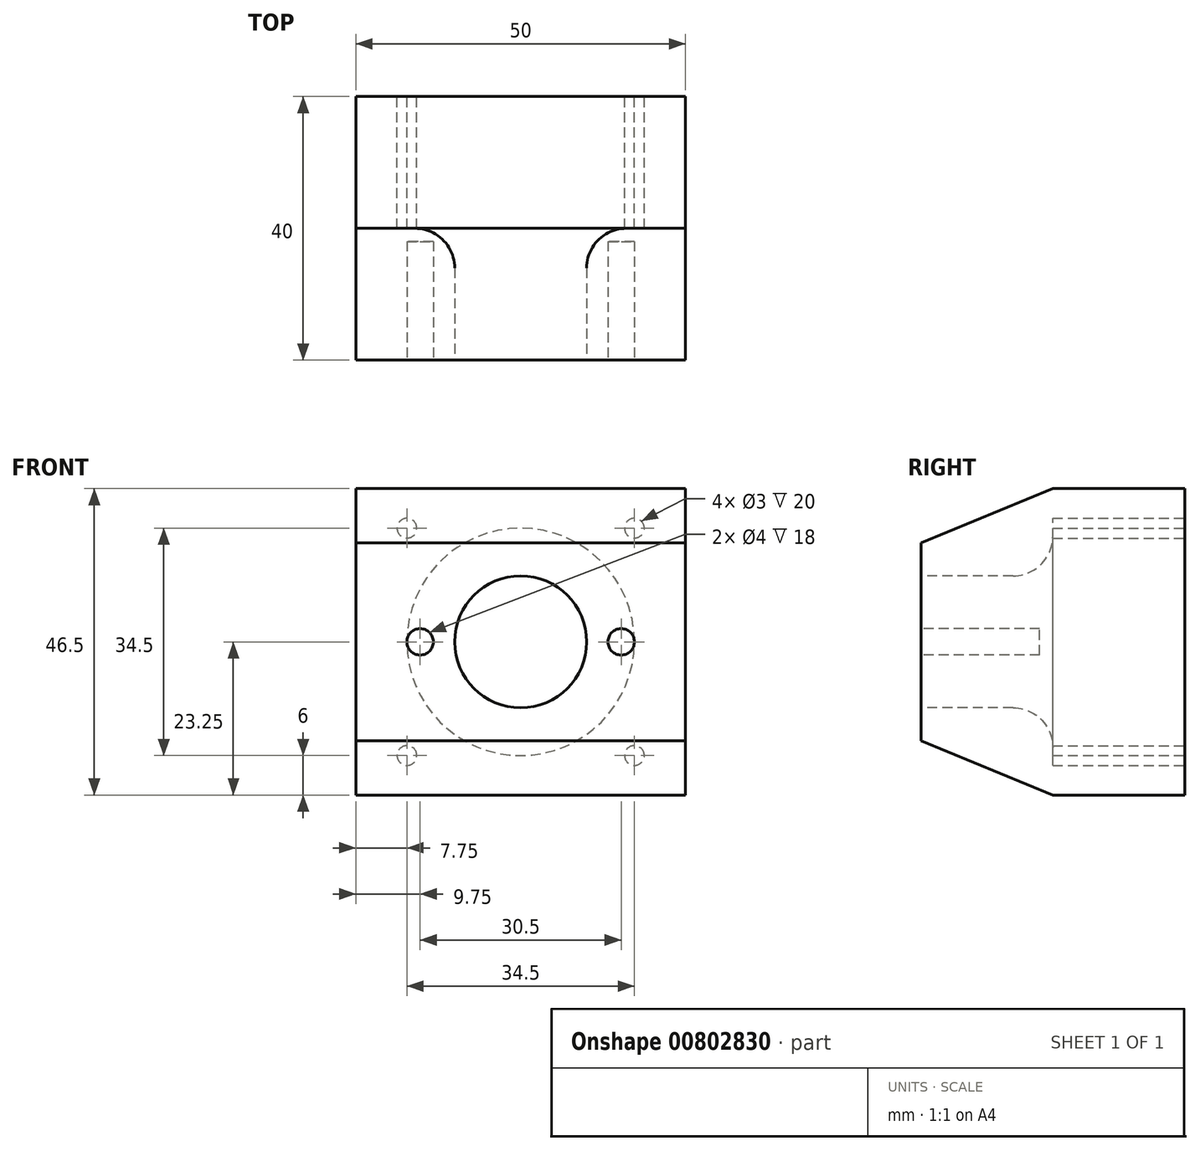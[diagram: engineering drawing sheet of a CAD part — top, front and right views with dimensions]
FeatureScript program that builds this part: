
annotation { "Feature Type Name" : "Feature", "Feature Type Description" : "" }
export const myFeature = defineFeature(function(context is Context, id is Id, definition is map)
    precondition{}
    {
        {
            var Q0;
            Q0=qCreatedBy(makeId("Front.planeOp"),FACE);
            var sketch = newSketch(context, id + "F0", { "sketchPlane" : qUnion([Q0])});
            skLineSegment(sketch, "E0.bottom", {"start": v(17.25, -17.25) * mm, "end": v(-17.25, -17.25) * mm});
            skLineSegment(sketch, "E0.top", {"start": v(17.25, 17.25) * mm, "end": v(-17.25, 17.25) * mm});
            skLineSegment(sketch, "E0.left", {"start": v(17.25, -17.25) * mm, "end": v(17.25, 17.25) * mm});
            skLineSegment(sketch, "E0.right", {"start": v(-17.25, -17.25) * mm, "end": v(-17.25, 17.25) * mm});
            skPoint(sketch, "E0.middle", {"position": v(0, 0) * mm});
            skCircle(sketch, "E1", {"center": v(-17.25, -17.25) * mm, "radius": 1.5 * mm});
            skCircle(sketch, "E2", {"center": v(17.25, -17.25) * mm, "radius": 1.5 * mm});
            skCircle(sketch, "E3", {"center": v(-17.25, 17.25) * mm, "radius": 1.5 * mm});
            skCircle(sketch, "E4", {"center": v(17.25, 17.25) * mm, "radius": 1.5 * mm});
            skLineSegment(sketch, "E5.bottom", {"start": v(23.25, -23.25) * mm, "end": v(-23.25, -23.25) * mm});
            skLineSegment(sketch, "E5.top", {"start": v(23.25, 23.25) * mm, "end": v(-23.25, 23.25) * mm});
            skLineSegment(sketch, "E5.left", {"start": v(23.25, -23.25) * mm, "end": v(23.25, 23.25) * mm});
            skLineSegment(sketch, "E5.right", {"start": v(-23.25, -23.25) * mm, "end": v(-23.25, 23.25) * mm});
            skCircle(sketch, "E6", {"center": v(0, 0) * mm, "radius": 17.25 * mm});
            skSolve(sketch);
        }
        {
            var Q0;
            Q0=makeQuery(id+"F0.imprint","IMPRINT",FACE,{"disambiguationData":[TD([[makeQuery(id+"F0.imprint","IMPRINT",EDGE,{"derivedFrom":sQuery(id+"F0.wireOp",EDGE,"E5.bottom")}),-1.0]])]});
            var Q1;
            {var subQ0=sQuery(id+"F0.wireOp",EDGE,"E6");var subQ1=sQuery(id+"F0.wireOp",EDGE,"E0.top");var subQ2=makeQuery(id+"F0.imprint","INTERSECT",VERTEX,{"derivedFrom":[subQ1,subQ0]});Q1=makeQuery(id+"F0.imprint","IMPRINT",FACE,{"disambiguationData":[TD([[makeQuery(id+"F0.imprint","IMPRINT",EDGE,{"disambiguationData":[TD([[subQ2,-1.0]])],"derivedFrom":subQ1}),1.0]])]});}
            var Q2;
            {var subQ0=sQuery(id+"F0.wireOp",EDGE,"E4");var subQ1=sQuery(id+"F0.wireOp",EDGE,"E0.top");var subQ2=makeQuery(id+"F0.imprint","INTERSECT",VERTEX,{"derivedFrom":[subQ1,subQ0]});Q2=makeQuery(id+"F0.imprint","IMPRINT",FACE,{"disambiguationData":[TD([[makeQuery(id+"F0.imprint","IMPRINT",EDGE,{"disambiguationData":[TD([[subQ2,-1.0]])],"derivedFrom":subQ1}),1.0]])]});}
            var Q3;
            {var subQ0=sQuery(id+"F0.wireOp",EDGE,"E6");var subQ1=sQuery(id+"F0.wireOp",EDGE,"E0.bottom");var subQ2=makeQuery(id+"F0.imprint","INTERSECT",VERTEX,{"derivedFrom":[subQ1,subQ0]});Q3=makeQuery(id+"F0.imprint","IMPRINT",FACE,{"disambiguationData":[TD([[makeQuery(id+"F0.imprint","IMPRINT",EDGE,{"disambiguationData":[TD([[subQ2,-1.0]])],"derivedFrom":subQ1}),-1.0]])]});}
            var Q4;
            {var subQ0=sQuery(id+"F0.wireOp",EDGE,"E2");var subQ1=sQuery(id+"F0.wireOp",EDGE,"E0.bottom");var subQ2=makeQuery(id+"F0.imprint","INTERSECT",VERTEX,{"derivedFrom":[subQ1,subQ0]});Q4=makeQuery(id+"F0.imprint","IMPRINT",FACE,{"disambiguationData":[TD([[makeQuery(id+"F0.imprint","IMPRINT",EDGE,{"disambiguationData":[TD([[subQ2,-1.0]])],"derivedFrom":subQ1}),-1.0]])]});}
            extrude(context, id + "F1", {"entities" : qUnion([Q0, Q1, Q2, Q3, Q4]), "depth" : 20 * mm, "offsetDistance" : 25 * mm});
        }
        {
            var Q0;
            Q0=qCreatedBy(makeId("Right.planeOp"),FACE);
            var sketch = newSketch(context, id + "F2", { "sketchPlane" : qUnion([Q0])});
            skPoint(sketch, "E7", {"position": v(-20, 23.25) * mm});
            skPoint(sketch, "E8", {"position": v(-20, 0) * mm});
            skPoint(sketch, "E9", {"position": v(-20, -23.25) * mm});
            skLineSegment(sketch, "E10", {"start": v(0, 0) * mm, "end": v(-93.52, 0) * mm});
            skPoint(sketch, "E11", {"position": v(-40, 0) * mm});
            skLineSegment(sketch, "E12", {"start": v(-40, 0) * mm, "end": v(-40, -15) * mm});
            skLineSegment(sketch, "E13", {"start": v(-40, -15) * mm, "end": v(-40, 15) * mm});
            skLineSegment(sketch, "E14", {"start": v(-20, 23.25) * mm, "end": v(-40, 15) * mm});
            skLineSegment(sketch, "E15", {"start": v(-40, -15) * mm, "end": v(-20, -23.25) * mm});
            skLineSegment(sketch, "E16", {"start": v(-20, 23.25) * mm, "end": v(-20, 0) * mm});
            skLineSegment(sketch, "E17", {"start": v(-20, -23.25) * mm, "end": v(-20, 0) * mm});
            skSolve(sketch);
        }
        {
            var Q0;
            {var subQ0=sQuery(id+"F2.wireOp",EDGE,"E13");var subQ1=sQuery(id+"F2.wireOp",EDGE,"E12");Q0=qUnion([makeQuery(id+"F2.imprint","IMPRINT",FACE,{"disambiguationData":[TD([[makeQuery(id+"F2.imprint","IMPRINT",EDGE,{"derivedFrom":subQ1}),1.0]])]}),makeQuery(id+"F2.imprint","IMPRINT",FACE,{"disambiguationData":[TD([[makeQuery(id+"F2.imprint","IMPRINT",EDGE,{"derivedFrom":subQ0}),-1.0]])]})]);}
            extrude(context, id + "F3", {"entities" : qUnion([Q0]), "operationType" : NewBodyOperationType.ADD, "depth" : 25 * mm, "offsetDistance" : 25 * mm, "hasSecondDirection" : true, "secondDirectionOppositeDirection" : true, "secondDirectionDepth" : 25 * mm});
        }
        {
            var Q0;
            Q0=makeQuery(id+"F3.opExtrude","SWEPT_FACE",FACE,{"disambiguationData":[OSD([sQuery(id+"F2.wireOp",EDGE,"E12"),sQuery(id+"F2.wireOp",EDGE,"E13")])]});
            var sketch = newSketch(context, id + "F4", { "sketchPlane" : qUnion([Q0])});
            skLineSegment(sketch, "E18", {"start": v(0, 0) * mm, "end": v(-15.25, 0) * mm});
            skLineSegment(sketch, "E19", {"start": v(-15.25, 0) * mm, "end": v(15.25, 0) * mm});
            skCircle(sketch, "E20", {"center": v(-15.25, 0) * mm, "radius": 2 * mm});
            skCircle(sketch, "E21", {"center": v(15.25, 0) * mm, "radius": 2 * mm});
            skSolve(sketch);
        }
        {
            var Q0;
            Q0 = qSketchRegion(id + "F4", true);
            extrude(context, id + "F5", {"entities" : qUnion([Q0]), "operationType" : NewBodyOperationType.REMOVE, "oppositeDirection" : true, "depth" : 18 * mm, "offsetDistance" : 25 * mm});
        }
        {
            var Q0;
            Q0=makeQuery(id+"F3.opExtrude","SWEPT_FACE",FACE,{"disambiguationData":[OSD([sQuery(id+"F2.wireOp",EDGE,"E12"),sQuery(id+"F2.wireOp",EDGE,"E13")])]});
            var sketch = newSketch(context, id + "F6", { "sketchPlane" : qUnion([Q0])});
            skCircle(sketch, "E22", {"center": v(0, 0) * mm, "radius": 10 * mm});
            skSolve(sketch);
        }
        {
            var Q0;
            Q0 = qSketchRegion(id + "F6", true);
            extrude(context, id + "F7", {"entities" : qUnion([Q0]), "operationType" : NewBodyOperationType.REMOVE, "oppositeDirection" : true, "depth" : 63.3 * mm, "offsetDistance" : 25 * mm});
        }
        {
            var Q0;
            Q0=makeQuery(id+"F7.boolean.opBoolean","INTERSECT",EDGE,{"derivedFrom":[makeQuery(id+"F3.boolean.opBoolean","SPLIT",FACE,{"disambiguationData":[TD([makeQuery(id+"F1.opExtrude","SWEPT_FACE",FACE,{"disambiguationData":[OSD([sQuery(id+"F0.wireOp",EDGE,"E6")])]})])],"derivedFrom":makeQuery(id+"F3.opExtrude","SWEPT_FACE",FACE,{"disambiguationData":[OSD([sQuery(id+"F2.wireOp",EDGE,"E16"),sQuery(id+"F2.wireOp",EDGE,"E17")])]})}),makeQuery(id+"F7.opExtrude","SWEPT_FACE",FACE,{"disambiguationData":[OSD([sQuery(id+"F6.wireOp",EDGE,"E22")])]})]});
            fillet(context, id + "F8", {"entities" : qUnion([Q0]), "radius" : 6.04 * mm, "tangentPropagation" : true, "allowEdgeOverflow" : false});
        }
        {
            var Q0;
            {var subQ0=sQuery(id+"F2.wireOp",EDGE,"E17");var subQ1=sQuery(id+"F2.wireOp",EDGE,"E16");Q0=makeQuery(id+"F3.boolean.opBoolean","SPLIT",FACE,{"disambiguationData":[TD([makeQuery(id+"F1.opExtrude","SWEPT_FACE",FACE,{"disambiguationData":[OSD([sQuery(id+"F0.wireOp",EDGE,"E5.right")])]})])],"derivedFrom":makeQuery(id+"F3.opExtrude","SWEPT_FACE",FACE,{"disambiguationData":[OSD([subQ1,subQ0])]})});}
            var Q1;
            {var subQ1=sQuery(id+"F2.wireOp",EDGE,"E17");var subQ2=sQuery(id+"F2.wireOp",EDGE,"E16");Q1=makeQuery(id+"F3.boolean.opBoolean","SPLIT",FACE,{"disambiguationData":[TD([makeQuery(id+"F1.opExtrude","SWEPT_FACE",FACE,{"disambiguationData":[OSD([sQuery(id+"F0.wireOp",EDGE,"E5.left")])]})])],"derivedFrom":makeQuery(id+"F3.opExtrude","SWEPT_FACE",FACE,{"disambiguationData":[OSD([subQ2,subQ1])]})});}
            extrude(context, id + "F9", {"entities" : qUnion([Q0, Q1]), "operationType" : NewBodyOperationType.ADD, "depth" : 30 * mm, "offsetDistance" : 25 * mm});
        }
        {
            var Q0;
            {var subQ0=sQuery(id+"F2.wireOp",EDGE,"E17");var subQ1=sQuery(id+"F2.wireOp",EDGE,"E16");Q0=makeQuery(id+"F9.opExtrude","CAP_FACE",FACE,{"disambiguationData":[OSD([subQ1,subQ0]),TDD([makeQuery(id+"F3.boolean.opBoolean","SPLIT",FACE,{"disambiguationData":[TD([makeQuery(id+"F1.opExtrude","SWEPT_FACE",FACE,{"disambiguationData":[OSD([sQuery(id+"F0.wireOp",EDGE,"E5.right")])]})])],"derivedFrom":makeQuery(id+"F3.opExtrude","SWEPT_FACE",FACE,{"disambiguationData":[OSD([subQ1,subQ0])]})})])],"isStart":false});}
            var Q1;
            {var subQ1=sQuery(id+"F2.wireOp",EDGE,"E17");var subQ2=sQuery(id+"F2.wireOp",EDGE,"E16");Q1=makeQuery(id+"F9.opExtrude","CAP_FACE",FACE,{"disambiguationData":[OSD([subQ2,subQ1]),TDD([makeQuery(id+"F3.boolean.opBoolean","SPLIT",FACE,{"disambiguationData":[TD([makeQuery(id+"F1.opExtrude","SWEPT_FACE",FACE,{"disambiguationData":[OSD([sQuery(id+"F0.wireOp",EDGE,"E5.left")])]})])],"derivedFrom":makeQuery(id+"F3.opExtrude","SWEPT_FACE",FACE,{"disambiguationData":[OSD([subQ2,subQ1])]})})])],"isStart":false});}
            extrude(context, id + "F10", {"entities" : qUnion([Q0, Q1]), "operationType" : NewBodyOperationType.REMOVE, "oppositeDirection" : true, "depth" : 10 * mm, "offsetDistance" : 25 * mm});
        }
    });
